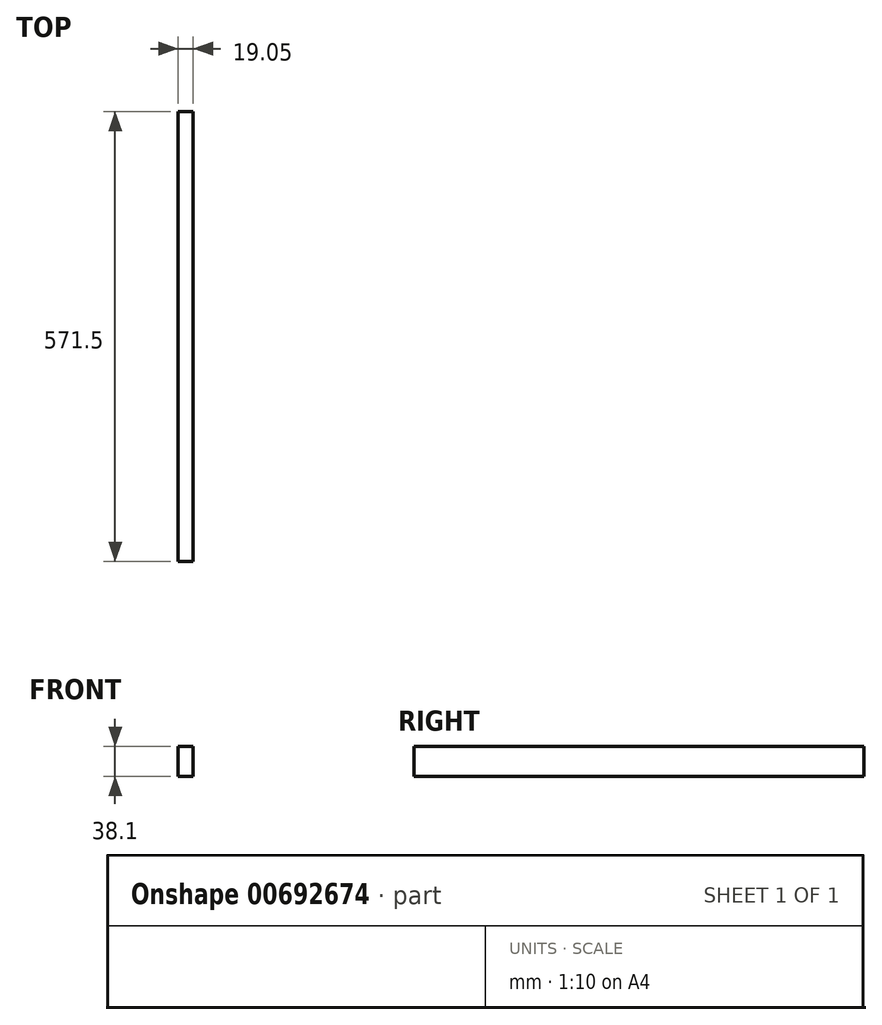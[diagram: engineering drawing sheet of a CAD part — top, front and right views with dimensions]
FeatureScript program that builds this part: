
annotation { "Feature Type Name" : "Feature", "Feature Type Description" : "" }
export const myFeature = defineFeature(function(context is Context, id is Id, definition is map)
    precondition{}
    {
        {
            var Q0;
            Q0=qCreatedBy(makeId("Top.planeOp"),FACE);
            var sketch = newSketch(context, id + "F0", { "sketchPlane" : qUnion([Q0])});
            skLineSegment(sketch, "E0.bottom", {"start": v(11.68, 474.38) * mm, "end": v(30.73, 474.38) * mm});
            skLineSegment(sketch, "E0.top", {"start": v(11.68, -97.12) * mm, "end": v(30.73, -97.12) * mm});
            skLineSegment(sketch, "E0.left", {"start": v(11.68, 474.38) * mm, "end": v(11.68, -97.12) * mm});
            skLineSegment(sketch, "E0.right", {"start": v(30.73, 474.38) * mm, "end": v(30.73, -97.12) * mm});
            skSolve(sketch);
        }
        {
            var Q0;
            Q0=makeQuery(id+"F0.imprint","IMPRINT",FACE,{"disambiguationData":[TD([[makeQuery(id+"F0.imprint","IMPRINT",EDGE,{"derivedFrom":sQuery(id+"F0.wireOp",EDGE,"E0.bottom")}),-1.0]])]});
            extrude(context, id + "F1", {"entities" : qUnion([Q0]), "depth" : 31.75 * mm, "offsetDistance" : 25.4 * mm});
        }
        {
            var Q0;
            Q0=makeQuery(id+"F1.opExtrude","CAP_FACE",FACE,{"disambiguationData":[OSD([sQuery(id+"F0.wireOp",EDGE,"E0.bottom"),sQuery(id+"F0.wireOp",EDGE,"E0.top"),sQuery(id+"F0.wireOp",EDGE,"E0.left"),sQuery(id+"F0.wireOp",EDGE,"E0.right")])],"isStart":true});
            extrude(context, id + "F2", {"entities" : qUnion([Q0]), "operationType" : NewBodyOperationType.ADD, "depth" : 6.35 * mm, "offsetDistance" : 25.4 * mm});
        }
    });
